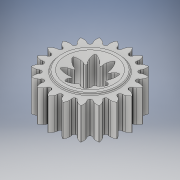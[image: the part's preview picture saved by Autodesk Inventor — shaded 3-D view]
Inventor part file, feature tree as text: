
AUTODESK INVENTOR PART (.ipt)
format: ipt  version: 2017 (Build 210142000, 142)  size: 867,840 bytes
history: native  units: in
note: dims shown in document units (in); Inventor stores cm internally (conversion verified against a paired STEP export)
features: extrude x5, sketch x5, other x2, fillet x2, pattern_circular x1, revolve x1
ambient origin geometry x8: Origin, YZ Plane, XZ Plane, XY Plane, X Axis, Y Axis, Z Axis, Center Point
bodies: Solid1 (feature_tree)
feature tree (16):
  other  "Table"
  other  "mId-01"
  extrude  "Extrusion9"  Depth=0.215in TaperAngle=0.0deg
  extrude  "Extrusion10"  Depth=0.0295in
  fillet  "Fillet5"  Radius=3.937in
  pattern_circular  "Circular Pattern4"  [2 undecoded]
  extrude  "Extrusion11"  Depth=0.005in
  revolve  "Revolution1"  Angle=360.0deg
  extrude  "Extrusion12"  Depth=0.005in
  extrude  "Extrusion13"  Depth=0.005in TaperAngle=0.0deg
  fillet  "Fillet6"  [1 undecoded]
  sketch  "Sketch12"  dims[d43=0.0271in d61=0.0295in d62=17.8955in]
  sketch  "Sketch13"  dims[d63=3.937in d65=1.0in d66=0.0in]
  sketch  "Sketch14"  dims[d71=0.055in d72=0.003in d73=0.0015in d74=0.2576in d75=0.0275in d76=0.074in d77=0.074in d78=0.0354in d79=0.043in d81=0.0108in d82=0.0177in d83=0.0144in d84=0.021in d85=0.0105in d86=0.0232in d87=0.0759in d89=0.0295in d90=17.8955in d91=3.937in]
  sketch  "Sketch15"  dims[d95=0.043in d96=0.0125in d97=7.874in d98=360.0deg d100=0.005in d101=1.0in d102=0.0in d106=22.5deg d107=90.0deg d108=0.15in d109=0.0in d110=0.35in d111=1.0in d112=0.01in d113=0.0in d114=0.35in d115=1.0in d116=0.01in d117=0.0in d118=0.005in]
  sketch  "Sketch11"  dims[d40=0.4695in d41=0.215in d42=0.0in]
note: 3 required parameter values undecoded (feature->parameter linkage not recoverable at this tier; creation-order binding heuristic only, values carry confidence <= 0.55)
